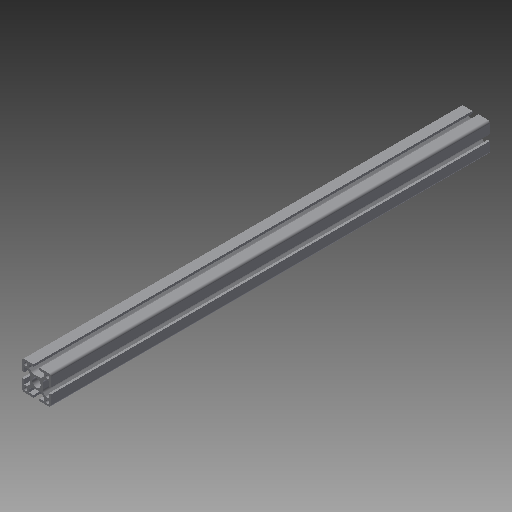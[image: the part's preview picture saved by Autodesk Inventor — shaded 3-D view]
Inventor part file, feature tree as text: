
AUTODESK INVENTOR PART (.ipt)
format: ipt  version: 2018 (Build 220112000, 112)  size: 222,720 bytes
history: native  units: mm
features: other x42, sketch x5, hole x4, extrude x1
ambient origin geometry x8: Origin, YZ Plane, XZ Plane, XY Plane, X Axis, Y Axis, Z Axis, Center Point
bodies: Solid1 (feature_tree)
feature tree (52):
  extrude  "Extrusion1"  [1 undecoded]
  hole  "Drilling 1"  [1 undecoded]
  hole  "Drilling 2"  [1 undecoded]
  hole  "Drilling 3"  [1 undecoded]
  hole  "Drilling 4"  [1 undecoded]
  other  "side_4d_XY"
  other  "side_4d_YZ"
  other  "side_4d_ZX"
  other  "side_4d_X"
  other  "side_4d_Y"
  other  "side_4d_Z"
  other  "side_4d_Center"
  other  "side_1a_XY"
  other  "side_1a_YZ"
  other  "side_1a_ZX"
  other  "side_1a_X"
  other  "side_1a_Y"
  other  "side_1a_Z"
  other  "side_1a_Center"
  other  "side_2b_XY"
  other  "side_2b_YZ"
  other  "side_2b_ZX"
  other  "side_2b_X"
  other  "side_2b_Y"
  other  "side_2b_Z"
  other  "side_2b_Center"
  other  "side_3c_XY"
  other  "side_3c_YZ"
  other  "side_3c_ZX"
  other  "side_3c_X"
  other  "side_3c_Y"
  other  "side_3c_Z"
  other  "side_3c_Center"
  other  "end_XY"
  other  "end_YZ"
  other  "end_ZX"
  other  "end_X"
  other  "end_Y"
  other  "end_Z"
  other  "end_Center"
  other  "start_XY"
  other  "start_YZ"
  other  "start_ZX"
  other  "start_X"
  other  "start_Y"
  other  "start_Z"
  other  "start_Center"
  sketch  "Skizze_1"  dims[d0=609.8mm d1=0.0mm]
  sketch  "Sketch2"  dims[d2=5.0mm d3=6.0mm d4=4.0mm d5=2.0mm d6=90.0deg d7=6000.0mm d8=0.0mm]
  sketch  "Sketch3"  dims[d9=5.0mm d10=6.0mm d11=4.0mm d12=2.0mm d13=90.0deg d14=6000.0mm d15=0.0mm]
  sketch  "Sketch4"  dims[d16=5.0mm d17=6.0mm d18=4.0mm d19=2.0mm d20=90.0deg d21=6000.0mm d22=0.0mm]
  sketch  "Sketch5"  dims[d23=5.0mm d24=6.0mm d25=4.0mm d26=2.0mm d27=90.0deg d28=6000.0mm d29=0.0mm]
note: 5 required parameter values undecoded (feature->parameter linkage not recoverable at this tier; creation-order binding heuristic only, values carry confidence <= 0.55)
